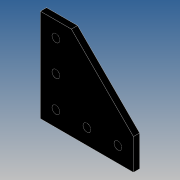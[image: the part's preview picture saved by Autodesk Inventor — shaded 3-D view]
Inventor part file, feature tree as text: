
AUTODESK INVENTOR PART (.ipt)
format: ipt  version: 2021 (Build 250183000, 183)  size: 148,480 bytes
history: native  units: mm
features: other x2, extrude x1, sketch x1
ambient origin geometry x8: Origin, YZ Plane, XZ Plane, XY Plane, X Axis, Y Axis, Z Axis, Center Point
bodies: Body1 (feature_tree)
feature tree (4):
  other  "Sólido1"
  extrude  "Extrusión1"  Depth=60.0mm
  sketch  "Boceto1"  dims[d3=60.0mm d4=60.0mm d5=20.0mm d6=20.0mm d7=5.0mm d8=30.0mm d10=20.0mm d11=10.0mm d13=10.0mm d17=30.0mm d19=20.0mm d20=10.0mm d22=10.0mm d26=4.0mm d27=0.0mm]
  other  "Imagen1"
